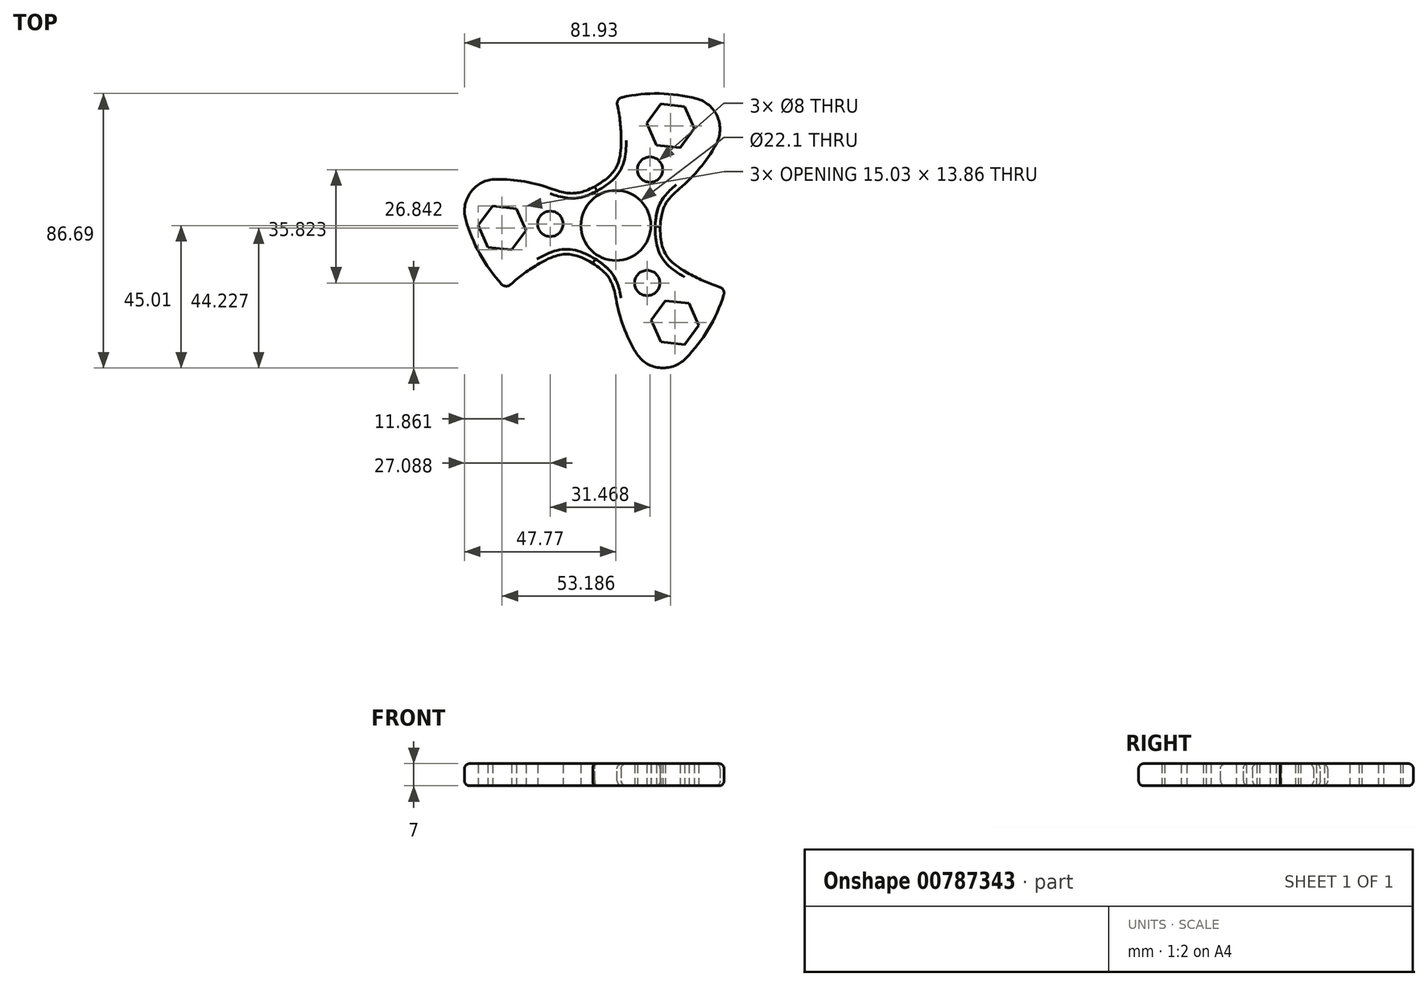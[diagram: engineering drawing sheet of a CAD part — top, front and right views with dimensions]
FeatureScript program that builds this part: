
annotation { "Feature Type Name" : "Feature", "Feature Type Description" : "" }
export const myFeature = defineFeature(function(context is Context, id is Id, definition is map)
    precondition{}
    {
        {
            var Q0;
            Q0=qCreatedBy(makeId("Top.planeOp"),FACE);
            var sketch = newSketch(context, id + "F0", { "sketchPlane" : qUnion([Q0])});
            skCircle(sketch, "E0", {"center": v(0, 0) * mm, "radius": 14 * mm});
            skArc(sketch, "E1", {"start": v(0, 14) * mm, "mid": v(1.66, 27) * mm, "end": v(0, 40) * mm});
            skPoint(sketch, "E2", {"position": v(0, 40) * mm});
            skLineSegment(sketch, "E3", {"start": v(0, 0) * mm, "end": v(36, 36) * mm, "construction": true});
            skPoint(sketch, "E4", {"position": v(36, 36) * mm});
            skArc(sketch, "E5.trimOffspring", {"start": v(36, 36) * mm, "mid": v(18.37, 41.37) * mm, "end": v(0, 40) * mm});
            skArc(sketch, "E6.trimOffspring", {"start": v(12.46, 6.39) * mm, "mid": v(27.14, 18.88) * mm, "end": v(36, 36) * mm});
            skCircle(sketch, "E7", {"center": v(0, 0) * mm, "radius": 11.05 * mm});
            skCircle(sketch, "E8.cCircle", {"center": v(17.28, 31.5) * mm, "radius": 6.55 * mm, "construction": true});
            skLineSegment(sketch, "E8.0", {"start": v(24.8, 30.65) * mm, "end": v(20.31, 24.56) * mm});
            skLineSegment(sketch, "E8.1", {"start": v(20.31, 24.56) * mm, "end": v(12.8, 25.4) * mm});
            skLineSegment(sketch, "E8.2", {"start": v(12.8, 25.4) * mm, "end": v(9.76, 32.33) * mm});
            skLineSegment(sketch, "E8.3", {"start": v(9.76, 32.33) * mm, "end": v(14.24, 38.42) * mm});
            skLineSegment(sketch, "E8.4", {"start": v(14.24, 38.42) * mm, "end": v(21.76, 37.58) * mm});
            skLineSegment(sketch, "E8.5", {"start": v(21.76, 37.58) * mm, "end": v(24.8, 30.65) * mm});
            skPoint(sketch, "E8.0.midPoint", {"position": v(22.55, 27.6) * mm});
            skCircle(sketch, "E9", {"center": v(10.79, 17.65) * mm, "radius": 4 * mm});
            skLineSegment(sketch, "E10", {"start": v(18, 38) * mm, "end": v(17.28, 31.5) * mm, "construction": true});
            skLineSegment(sketch, "E11", {"start": v(0, 14) * mm, "end": v(12.46, 6.39) * mm, "construction": true});
            skLineSegment(sketch, "E12", {"start": v(6.23, 10.2) * mm, "end": v(15.34, 25.11) * mm, "construction": true});
            skLineSegment(sketch, "E13", {"start": v(36, 36) * mm, "end": v(0, 40) * mm, "construction": true});
            skLineSegment(sketch, "E14.1.0", {"start": v(-28.4, -1.62) * mm, "end": v(-32.87, -7.71) * mm});
            skLineSegment(sketch, "E14.1.1", {"start": v(-41.9, -3.41) * mm, "end": v(-35.9, -0.78) * mm, "construction": true});
            skCircle(sketch, "E14.1.2", {"center": v(-20.68, 0.51) * mm, "radius": 4 * mm});
            skCircle(sketch, "E14.1.3", {"center": v(-35.9, -0.78) * mm, "radius": 6.55 * mm, "construction": true});
            skArc(sketch, "E14.1.4", {"start": v(-49.18, 13.18) * mm, "mid": v(-45.02, -4.77) * mm, "end": v(-34.64, -20) * mm});
            skArc(sketch, "E14.1.5", {"start": v(-11.76, 7.6) * mm, "mid": v(-29.92, 14.06) * mm, "end": v(-49.18, 13.18) * mm});
            skLineSegment(sketch, "E14.1.6", {"start": v(0, 0) * mm, "end": v(-49.18, 13.18) * mm, "construction": true});
            skPoint(sketch, "E14.1.7", {"position": v(-35.19, 5.73) * mm});
            skLineSegment(sketch, "E14.1.8", {"start": v(-31.43, 5.3) * mm, "end": v(-28.4, -1.62) * mm});
            skLineSegment(sketch, "E14.1.9", {"start": v(-49.18, 13.18) * mm, "end": v(-34.64, -20) * mm, "construction": true});
            skPoint(sketch, "E14.1.10", {"position": v(-49.18, 13.18) * mm});
            skLineSegment(sketch, "E14.1.11", {"start": v(-11.94, 0.3) * mm, "end": v(-29.42, 0.73) * mm, "construction": true});
            skLineSegment(sketch, "E14.1.12", {"start": v(-32.87, -7.71) * mm, "end": v(-40.4, -6.88) * mm});
            skLineSegment(sketch, "E14.1.13", {"start": v(-40.4, -6.88) * mm, "end": v(-43.43, 0.05) * mm});
            skLineSegment(sketch, "E14.1.14", {"start": v(-38.94, 6.14) * mm, "end": v(-31.43, 5.3) * mm});
            skLineSegment(sketch, "E14.1.15", {"start": v(-43.43, 0.05) * mm, "end": v(-38.94, 6.14) * mm});
            skArc(sketch, "E14.1.16", {"start": v(-12.12, -7) * mm, "mid": v(-24.21, -12.06) * mm, "end": v(-34.64, -20) * mm});
            skLineSegment(sketch, "E14.2.0", {"start": v(15.6, -23.78) * mm, "end": v(23.11, -24.61) * mm});
            skLineSegment(sketch, "E14.2.1", {"start": v(23.9, -34.59) * mm, "end": v(18.63, -30.7) * mm, "construction": true});
            skCircle(sketch, "E14.2.2", {"center": v(9.9, -18.17) * mm, "radius": 4 * mm});
            skCircle(sketch, "E14.2.3", {"center": v(18.63, -30.7) * mm, "radius": 6.55 * mm, "construction": true});
            skArc(sketch, "E14.2.4", {"start": v(13.18, -49.18) * mm, "mid": v(26.64, -36.6) * mm, "end": v(34.64, -20) * mm});
            skArc(sketch, "E14.2.5", {"start": v(-0.7, -13.98) * mm, "mid": v(2.78, -32.94) * mm, "end": v(13.18, -49.18) * mm});
            skLineSegment(sketch, "E14.2.6", {"start": v(0, 0) * mm, "end": v(13.18, -49.18) * mm, "construction": true});
            skPoint(sketch, "E14.2.7", {"position": v(12.63, -33.34) * mm});
            skLineSegment(sketch, "E14.2.8", {"start": v(11.12, -29.87) * mm, "end": v(15.6, -23.78) * mm});
            skLineSegment(sketch, "E14.2.9", {"start": v(13.18, -49.18) * mm, "end": v(34.64, -20) * mm, "construction": true});
            skPoint(sketch, "E14.2.10", {"position": v(13.18, -49.18) * mm});
            skLineSegment(sketch, "E14.2.11", {"start": v(5.71, -10.5) * mm, "end": v(14.08, -25.85) * mm, "construction": true});
            skLineSegment(sketch, "E14.2.12", {"start": v(23.11, -24.61) * mm, "end": v(26.15, -31.54) * mm});
            skLineSegment(sketch, "E14.2.13", {"start": v(26.15, -31.54) * mm, "end": v(21.67, -37.63) * mm});
            skLineSegment(sketch, "E14.2.14", {"start": v(14.15, -36.8) * mm, "end": v(11.12, -29.87) * mm});
            skLineSegment(sketch, "E14.2.15", {"start": v(21.67, -37.63) * mm, "end": v(14.15, -36.8) * mm});
            skArc(sketch, "E14.2.16", {"start": v(12.12, -7) * mm, "mid": v(22.55, -14.94) * mm, "end": v(34.64, -20) * mm});
            skSolve(sketch);
        }
        {
            var Q0;
            Q0=qSketchRegion(id+"F0",true);
            extrude(context, id + "F1", {"entities" : qUnion([Q0]), "depth" : 7 * mm, "offsetDistance" : 25 * mm});
        }
        {
            var Q0;
            Q0=makeQuery(id+"FwcY3XiP80TZzvs_1.opPattern","COPY",EDGE,{"derivedFrom":makeQuery(id+"F1.opExtrude","SWEPT_EDGE",EDGE,{"disambiguationData":[OSD([sQuery(id+"F0.wireOp",EDGE,"E5.trimOffspring"),sQuery(id+"F0.wireOp",EDGE,"E6.trimOffspring")])]}),"instanceName":"1"});
            var Q1;
            Q1=makeQuery(id+"FwcY3XiP80TZzvs_1.opPattern","COPY",EDGE,{"derivedFrom":makeQuery(id+"F1.opExtrude","SWEPT_EDGE",EDGE,{"disambiguationData":[OSD([sQuery(id+"F0.wireOp",EDGE,"E5.trimOffspring"),sQuery(id+"F0.wireOp",EDGE,"E6.trimOffspring")])]}),"instanceName":"3"});
            var Q2;
            Q2=makeQuery(id+"FwcY3XiP80TZzvs_1.opPattern","COPY",EDGE,{"derivedFrom":makeQuery(id+"F1.opExtrude","SWEPT_EDGE",EDGE,{"disambiguationData":[OSD([sQuery(id+"F0.wireOp",EDGE,"E5.trimOffspring"),sQuery(id+"F0.wireOp",EDGE,"E6.trimOffspring")])]}),"instanceName":"2"});
            var Q3;
            Q3=makeQuery(id+"F1.opExtrude","SWEPT_EDGE",EDGE,{"disambiguationData":[OSD([sQuery(id+"F0.wireOp",EDGE,"E5.trimOffspring"),sQuery(id+"F0.wireOp",EDGE,"E6.trimOffspring")])]});
            var Q4;
            Q4=makeQuery(id+"F1.opExtrude","SWEPT_EDGE",EDGE,{"disambiguationData":[OSD([sQuery(id+"F0.wireOp",EDGE,"E14.1.4"),sQuery(id+"F0.wireOp",EDGE,"E14.1.5")])]});
            var Q5;
            Q5=makeQuery(id+"F1.opExtrude","SWEPT_EDGE",EDGE,{"disambiguationData":[OSD([sQuery(id+"F0.wireOp",EDGE,"E14.2.4"),sQuery(id+"F0.wireOp",EDGE,"E14.2.5")])]});
            fillet(context, id + "F2", {"entities" : qUnion([Q0, Q1, Q2, Q3, Q4, Q5]), "radius" : 10 * mm, "tangentPropagation" : true, "allowEdgeOverflow" : false});
        }
        {
            var Q0;
            Q0=makeQuery(id+"FwcY3XiP80TZzvs_1.opPattern","COPY",EDGE,{"derivedFrom":makeQuery(id+"F1.opExtrude","SWEPT_EDGE",EDGE,{"disambiguationData":[OSD([sQuery(id+"F0.wireOp",EDGE,"E1"),sQuery(id+"F0.wireOp",EDGE,"E5.trimOffspring")])]}),"instanceName":"1"});
            var Q1;
            Q1=makeQuery(id+"F1.opExtrude","SWEPT_EDGE",EDGE,{"disambiguationData":[OSD([sQuery(id+"F0.wireOp",EDGE,"E1"),sQuery(id+"F0.wireOp",EDGE,"E5.trimOffspring")])]});
            var Q2;
            Q2=makeQuery(id+"FwcY3XiP80TZzvs_1.opPattern","COPY",EDGE,{"derivedFrom":makeQuery(id+"F1.opExtrude","SWEPT_EDGE",EDGE,{"disambiguationData":[OSD([sQuery(id+"F0.wireOp",EDGE,"E1"),sQuery(id+"F0.wireOp",EDGE,"E5.trimOffspring")])]}),"instanceName":"3"});
            var Q3;
            Q3=makeQuery(id+"FwcY3XiP80TZzvs_1.opPattern","COPY",EDGE,{"derivedFrom":makeQuery(id+"F1.opExtrude","SWEPT_EDGE",EDGE,{"disambiguationData":[OSD([sQuery(id+"F0.wireOp",EDGE,"E1"),sQuery(id+"F0.wireOp",EDGE,"E5.trimOffspring")])]}),"instanceName":"2"});
            var Q4;
            Q4=makeQuery(id+"F1.opExtrude","SWEPT_EDGE",EDGE,{"disambiguationData":[OSD([sQuery(id+"F0.wireOp",EDGE,"E14.1.4"),sQuery(id+"F0.wireOp",EDGE,"E14.1.16")])]});
            var Q5;
            Q5=makeQuery(id+"F1.opExtrude","SWEPT_EDGE",EDGE,{"disambiguationData":[OSD([sQuery(id+"F0.wireOp",EDGE,"E14.2.4"),sQuery(id+"F0.wireOp",EDGE,"E14.2.16")])]});
            fillet(context, id + "F3", {"entities" : qUnion([Q0, Q1, Q2, Q3, Q4, Q5]), "radius" : 2 * mm, "tangentPropagation" : true, "allowEdgeOverflow" : false});
        }
        {
            var Q0;
            Q0=makeQuery(id+"F1.opExtrude","SWEPT_EDGE",EDGE,{"disambiguationData":[OSD([sQuery(id+"F0.wireOp",EDGE,"E0"),sQuery(id+"F0.wireOp",EDGE,"E14.2.16")])]});
            var Q1;
            Q1=makeQuery(id+"F1.opExtrude","SWEPT_EDGE",EDGE,{"disambiguationData":[OSD([sQuery(id+"F0.wireOp",EDGE,"E0"),sQuery(id+"F0.wireOp",EDGE,"E6.trimOffspring")])]});
            var Q2;
            Q2=makeQuery(id+"F1.opExtrude","SWEPT_EDGE",EDGE,{"disambiguationData":[OSD([sQuery(id+"F0.wireOp",EDGE,"E0"),sQuery(id+"F0.wireOp",EDGE,"E1")])]});
            var Q3;
            Q3=makeQuery(id+"F1.opExtrude","SWEPT_EDGE",EDGE,{"disambiguationData":[OSD([sQuery(id+"F0.wireOp",EDGE,"E0"),sQuery(id+"F0.wireOp",EDGE,"E14.1.5")])]});
            var Q4;
            Q4=makeQuery(id+"F1.opExtrude","SWEPT_EDGE",EDGE,{"disambiguationData":[OSD([sQuery(id+"F0.wireOp",EDGE,"E0"),sQuery(id+"F0.wireOp",EDGE,"E14.1.16")])]});
            var Q5;
            Q5=makeQuery(id+"F1.opExtrude","SWEPT_EDGE",EDGE,{"disambiguationData":[OSD([sQuery(id+"F0.wireOp",EDGE,"E0"),sQuery(id+"F0.wireOp",EDGE,"E14.2.5")])]});
            fillet(context, id + "F4", {"entities" : qUnion([Q0, Q1, Q2, Q3, Q4, Q5]), "radius" : 17 * mm, "rho" : .6, "crossSection" : FilletCrossSection.CONIC, "allowEdgeOverflow" : false});
        }
        {
            var Q0;
            Q0=makeQuery(id+"F1.opExtrude","CAP_EDGE",EDGE,{"disambiguationData":[OSD([sQuery(id+"F0.wireOp",EDGE,"E14.1.4")])],"isStart":false});
            var Q1;
            Q1=makeQuery(id+"F1.opExtrude","CAP_EDGE",EDGE,{"disambiguationData":[OSD([sQuery(id+"F0.wireOp",EDGE,"E5.trimOffspring")])],"isStart":false});
            var Q2;
            Q2=makeQuery(id+"F1.opExtrude","CAP_EDGE",EDGE,{"disambiguationData":[OSD([sQuery(id+"F0.wireOp",EDGE,"E14.2.4")])],"isStart":false});
            var Q3;
            Q3=makeQuery(id+"F1.opExtrude","CAP_EDGE",EDGE,{"disambiguationData":[OSD([sQuery(id+"F0.wireOp",EDGE,"b6dc6e87-022c-4587-a6bb-449be63d97bc.2.0")])],"isStart":false});
            var Q4;
            Q4=makeQuery(id+"F1.opExtrude","CAP_EDGE",EDGE,{"disambiguationData":[OSD([sQuery(id+"F0.wireOp",EDGE,"b6dc6e87-022c-4587-a6bb-449be63d97bc.2.2")])],"isStart":false});
            var Q5;
            Q5=makeQuery(id+"F1.opExtrude","CAP_EDGE",EDGE,{"disambiguationData":[OSD([sQuery(id+"F0.wireOp",EDGE,"b6dc6e87-022c-4587-a6bb-449be63d97bc.2.1")])],"isStart":false});
            var Q6;
            Q6=makeQuery(id+"F1.opExtrude","CAP_EDGE",EDGE,{"disambiguationData":[OSD([sQuery(id+"F0.wireOp",EDGE,"b6dc6e87-022c-4587-a6bb-449be63d97bc.2.3")])],"isStart":false});
            var Q7;
            {var subQ0=sQuery(id+"F0.wireOp",EDGE,"E14.2.5");var subQ1=sQuery(id+"F0.wireOp",EDGE,"E14.2.4");Q7=makeQuery(id+"F2.opFillet","BLEND_EDGE",EDGE,{"blendedFrom":[makeQuery(id+"F1.opExtrude","SWEPT_EDGE",EDGE,{"disambiguationData":[OSD([subQ1,subQ0])]}),makeQuery(id+"F1.opExtrude","CAP_FACE",FACE,{"disambiguationData":[OSD([sQuery(id+"F0.wireOp",EDGE,"E0"),sQuery(id+"F0.wireOp",EDGE,"E1"),sQuery(id+"F0.wireOp",EDGE,"E5.trimOffspring"),sQuery(id+"F0.wireOp",EDGE,"E6.trimOffspring"),sQuery(id+"F0.wireOp",EDGE,"E8.0"),sQuery(id+"F0.wireOp",EDGE,"E8.1"),sQuery(id+"F0.wireOp",EDGE,"E8.2"),sQuery(id+"F0.wireOp",EDGE,"E8.3"),sQuery(id+"F0.wireOp",EDGE,"E8.4"),sQuery(id+"F0.wireOp",EDGE,"E8.5"),sQuery(id+"F0.wireOp",EDGE,"E9"),sQuery(id+"F0.wireOp",EDGE,"E14.1.0"),sQuery(id+"F0.wireOp",EDGE,"E14.1.2"),sQuery(id+"F0.wireOp",EDGE,"E14.1.4"),sQuery(id+"F0.wireOp",EDGE,"E14.1.5"),sQuery(id+"F0.wireOp",EDGE,"E14.1.8"),sQuery(id+"F0.wireOp",EDGE,"E14.1.12"),sQuery(id+"F0.wireOp",EDGE,"E14.1.13"),sQuery(id+"F0.wireOp",EDGE,"E14.1.14"),sQuery(id+"F0.wireOp",EDGE,"E14.1.15"),sQuery(id+"F0.wireOp",EDGE,"E14.1.16"),sQuery(id+"F0.wireOp",EDGE,"E14.2.0"),sQuery(id+"F0.wireOp",EDGE,"E14.2.2"),subQ1,subQ0,sQuery(id+"F0.wireOp",EDGE,"E14.2.8"),sQuery(id+"F0.wireOp",EDGE,"E14.2.12"),sQuery(id+"F0.wireOp",EDGE,"E14.2.13"),sQuery(id+"F0.wireOp",EDGE,"E14.2.14"),sQuery(id+"F0.wireOp",EDGE,"E14.2.15"),sQuery(id+"F0.wireOp",EDGE,"E14.2.16"),sQuery(id+"F0.wireOp",EDGE,"dOVvf4ZY-hfaG-VCGh-6djX-qI10KFZVYham"),sQuery(id+"F0.wireOp",EDGE,"qjIoeBWy-CccR-NzYj-1DTf-gikf3EaqEeLr"),sQuery(id+"F0.wireOp",EDGE,"2TvMucum-B2Yi-Opv7-W324-o2eA7hxeLcYX"),sQuery(id+"F0.wireOp",EDGE,"7mXubkyq-BCgf-0Zro-0wdY-kL4kbCmWapzR"),sQuery(id+"F0.wireOp",EDGE,"b6dc6e87-022c-4587-a6bb-449be63d97bc.1.0"),sQuery(id+"F0.wireOp",EDGE,"b6dc6e87-022c-4587-a6bb-449be63d97bc.1.1"),sQuery(id+"F0.wireOp",EDGE,"b6dc6e87-022c-4587-a6bb-449be63d97bc.1.2"),sQuery(id+"F0.wireOp",EDGE,"b6dc6e87-022c-4587-a6bb-449be63d97bc.1.3"),sQuery(id+"F0.wireOp",EDGE,"b6dc6e87-022c-4587-a6bb-449be63d97bc.2.0"),sQuery(id+"F0.wireOp",EDGE,"b6dc6e87-022c-4587-a6bb-449be63d97bc.2.1"),sQuery(id+"F0.wireOp",EDGE,"b6dc6e87-022c-4587-a6bb-449be63d97bc.2.2"),sQuery(id+"F0.wireOp",EDGE,"b6dc6e87-022c-4587-a6bb-449be63d97bc.2.3")])],"isStart":true})],"blendedInto":[makeQuery(id+"F1.opExtrude","CAP_FACE",FACE,{"disambiguationData":[OSD([sQuery(id+"F0.wireOp",EDGE,"E0"),sQuery(id+"F0.wireOp",EDGE,"E1"),sQuery(id+"F0.wireOp",EDGE,"E5.trimOffspring"),sQuery(id+"F0.wireOp",EDGE,"E6.trimOffspring"),sQuery(id+"F0.wireOp",EDGE,"E8.0"),sQuery(id+"F0.wireOp",EDGE,"E8.1"),sQuery(id+"F0.wireOp",EDGE,"E8.2"),sQuery(id+"F0.wireOp",EDGE,"E8.3"),sQuery(id+"F0.wireOp",EDGE,"E8.4"),sQuery(id+"F0.wireOp",EDGE,"E8.5"),sQuery(id+"F0.wireOp",EDGE,"E9"),sQuery(id+"F0.wireOp",EDGE,"E14.1.0"),sQuery(id+"F0.wireOp",EDGE,"E14.1.2"),sQuery(id+"F0.wireOp",EDGE,"E14.1.4"),sQuery(id+"F0.wireOp",EDGE,"E14.1.5"),sQuery(id+"F0.wireOp",EDGE,"E14.1.8"),sQuery(id+"F0.wireOp",EDGE,"E14.1.12"),sQuery(id+"F0.wireOp",EDGE,"E14.1.13"),sQuery(id+"F0.wireOp",EDGE,"E14.1.14"),sQuery(id+"F0.wireOp",EDGE,"E14.1.15"),sQuery(id+"F0.wireOp",EDGE,"E14.1.16"),sQuery(id+"F0.wireOp",EDGE,"E14.2.0"),sQuery(id+"F0.wireOp",EDGE,"E14.2.2"),subQ1,subQ0,sQuery(id+"F0.wireOp",EDGE,"E14.2.8"),sQuery(id+"F0.wireOp",EDGE,"E14.2.12"),sQuery(id+"F0.wireOp",EDGE,"E14.2.13"),sQuery(id+"F0.wireOp",EDGE,"E14.2.14"),sQuery(id+"F0.wireOp",EDGE,"E14.2.15"),sQuery(id+"F0.wireOp",EDGE,"E14.2.16"),sQuery(id+"F0.wireOp",EDGE,"dOVvf4ZY-hfaG-VCGh-6djX-qI10KFZVYham"),sQuery(id+"F0.wireOp",EDGE,"qjIoeBWy-CccR-NzYj-1DTf-gikf3EaqEeLr"),sQuery(id+"F0.wireOp",EDGE,"2TvMucum-B2Yi-Opv7-W324-o2eA7hxeLcYX"),sQuery(id+"F0.wireOp",EDGE,"7mXubkyq-BCgf-0Zro-0wdY-kL4kbCmWapzR"),sQuery(id+"F0.wireOp",EDGE,"b6dc6e87-022c-4587-a6bb-449be63d97bc.1.0"),sQuery(id+"F0.wireOp",EDGE,"b6dc6e87-022c-4587-a6bb-449be63d97bc.1.1"),sQuery(id+"F0.wireOp",EDGE,"b6dc6e87-022c-4587-a6bb-449be63d97bc.1.2"),sQuery(id+"F0.wireOp",EDGE,"b6dc6e87-022c-4587-a6bb-449be63d97bc.1.3"),sQuery(id+"F0.wireOp",EDGE,"b6dc6e87-022c-4587-a6bb-449be63d97bc.2.0"),sQuery(id+"F0.wireOp",EDGE,"b6dc6e87-022c-4587-a6bb-449be63d97bc.2.1"),sQuery(id+"F0.wireOp",EDGE,"b6dc6e87-022c-4587-a6bb-449be63d97bc.2.2"),sQuery(id+"F0.wireOp",EDGE,"b6dc6e87-022c-4587-a6bb-449be63d97bc.2.3")])],"isStart":true})]});}
            var Q8;
            Q8=makeQuery(id+"F1.opExtrude","CAP_EDGE",EDGE,{"disambiguationData":[OSD([sQuery(id+"F0.wireOp",EDGE,"E14.1.4")])],"isStart":true});
            var Q9;
            Q9=makeQuery(id+"F1.opExtrude","CAP_EDGE",EDGE,{"disambiguationData":[OSD([sQuery(id+"F0.wireOp",EDGE,"E5.trimOffspring")])],"isStart":true});
            var Q10;
            Q10=makeQuery(id+"F1.opExtrude","CAP_EDGE",EDGE,{"disambiguationData":[OSD([sQuery(id+"F0.wireOp",EDGE,"b6dc6e87-022c-4587-a6bb-449be63d97bc.1.3")])],"isStart":true});
            var Q11;
            Q11=makeQuery(id+"F1.opExtrude","CAP_EDGE",EDGE,{"disambiguationData":[OSD([sQuery(id+"F0.wireOp",EDGE,"b6dc6e87-022c-4587-a6bb-449be63d97bc.1.2")])],"isStart":true});
            var Q12;
            Q12=makeQuery(id+"F1.opExtrude","CAP_EDGE",EDGE,{"disambiguationData":[OSD([sQuery(id+"F0.wireOp",EDGE,"b6dc6e87-022c-4587-a6bb-449be63d97bc.1.1")])],"isStart":true});
            var Q13;
            Q13=makeQuery(id+"F1.opExtrude","CAP_EDGE",EDGE,{"disambiguationData":[OSD([sQuery(id+"F0.wireOp",EDGE,"b6dc6e87-022c-4587-a6bb-449be63d97bc.1.0")])],"isStart":true});
            var Q14;
            Q14=makeQuery(id+"F1.opExtrude","CAP_EDGE",EDGE,{"disambiguationData":[OSD([sQuery(id+"F0.wireOp",EDGE,"b6dc6e87-022c-4587-a6bb-449be63d97bc.2.3")])],"isStart":true});
            var Q15;
            Q15=makeQuery(id+"F1.opExtrude","CAP_EDGE",EDGE,{"disambiguationData":[OSD([sQuery(id+"F0.wireOp",EDGE,"b6dc6e87-022c-4587-a6bb-449be63d97bc.2.2")])],"isStart":true});
            var Q16;
            Q16=makeQuery(id+"F1.opExtrude","CAP_EDGE",EDGE,{"disambiguationData":[OSD([sQuery(id+"F0.wireOp",EDGE,"b6dc6e87-022c-4587-a6bb-449be63d97bc.2.1")])],"isStart":true});
            var Q17;
            Q17=makeQuery(id+"F1.opExtrude","CAP_EDGE",EDGE,{"disambiguationData":[OSD([sQuery(id+"F0.wireOp",EDGE,"b6dc6e87-022c-4587-a6bb-449be63d97bc.2.0")])],"isStart":true});
            var Q18;
            Q18=makeQuery(id+"F1.opExtrude","CAP_EDGE",EDGE,{"disambiguationData":[OSD([sQuery(id+"F0.wireOp",EDGE,"qjIoeBWy-CccR-NzYj-1DTf-gikf3EaqEeLr")])],"isStart":true});
            var Q19;
            Q19=makeQuery(id+"F1.opExtrude","CAP_EDGE",EDGE,{"disambiguationData":[OSD([sQuery(id+"F0.wireOp",EDGE,"dOVvf4ZY-hfaG-VCGh-6djX-qI10KFZVYham")])],"isStart":true});
            var Q20;
            Q20=makeQuery(id+"F1.opExtrude","CAP_EDGE",EDGE,{"disambiguationData":[OSD([sQuery(id+"F0.wireOp",EDGE,"2TvMucum-B2Yi-Opv7-W324-o2eA7hxeLcYX")])],"isStart":true});
            var Q21;
            Q21=makeQuery(id+"F1.opExtrude","CAP_EDGE",EDGE,{"disambiguationData":[OSD([sQuery(id+"F0.wireOp",EDGE,"7mXubkyq-BCgf-0Zro-0wdY-kL4kbCmWapzR")])],"isStart":true});
            var Q22;
            Q22=makeQuery(id+"F1.opExtrude","CAP_EDGE",EDGE,{"disambiguationData":[OSD([sQuery(id+"F0.wireOp",EDGE,"7mXubkyq-BCgf-0Zro-0wdY-kL4kbCmWapzR")])],"isStart":false});
            var Q23;
            Q23=makeQuery(id+"F1.opExtrude","CAP_EDGE",EDGE,{"disambiguationData":[OSD([sQuery(id+"F0.wireOp",EDGE,"2TvMucum-B2Yi-Opv7-W324-o2eA7hxeLcYX")])],"isStart":false});
            var Q24;
            Q24=makeQuery(id+"F1.opExtrude","CAP_EDGE",EDGE,{"disambiguationData":[OSD([sQuery(id+"F0.wireOp",EDGE,"dOVvf4ZY-hfaG-VCGh-6djX-qI10KFZVYham")])],"isStart":false});
            var Q25;
            Q25=makeQuery(id+"F1.opExtrude","CAP_EDGE",EDGE,{"disambiguationData":[OSD([sQuery(id+"F0.wireOp",EDGE,"b6dc6e87-022c-4587-a6bb-449be63d97bc.1.3")])],"isStart":false});
            var Q26;
            Q26=makeQuery(id+"F1.opExtrude","CAP_EDGE",EDGE,{"disambiguationData":[OSD([sQuery(id+"F0.wireOp",EDGE,"b6dc6e87-022c-4587-a6bb-449be63d97bc.1.1")])],"isStart":false});
            var Q27;
            Q27=makeQuery(id+"F1.opExtrude","CAP_EDGE",EDGE,{"disambiguationData":[OSD([sQuery(id+"F0.wireOp",EDGE,"b6dc6e87-022c-4587-a6bb-449be63d97bc.1.0")])],"isStart":false});
            var Q28;
            Q28=makeQuery(id+"F1.opExtrude","CAP_EDGE",EDGE,{"disambiguationData":[OSD([sQuery(id+"F0.wireOp",EDGE,"b6dc6e87-022c-4587-a6bb-449be63d97bc.1.2")])],"isStart":false});
            fillet(context, id + "F5", {"entities" : qUnion([Q0, Q1, Q2, Q3, Q4, Q5, Q6, Q7, Q8, Q9, Q10, Q11, Q12, Q13, Q14, Q15, Q16, Q17, Q18, Q19, Q20, Q21, Q22, Q23, Q24, Q25, Q26, Q27, Q28]), "radius" : 1.6 * mm, "tangentPropagation" : true, "allowEdgeOverflow" : false});
        }
    });
